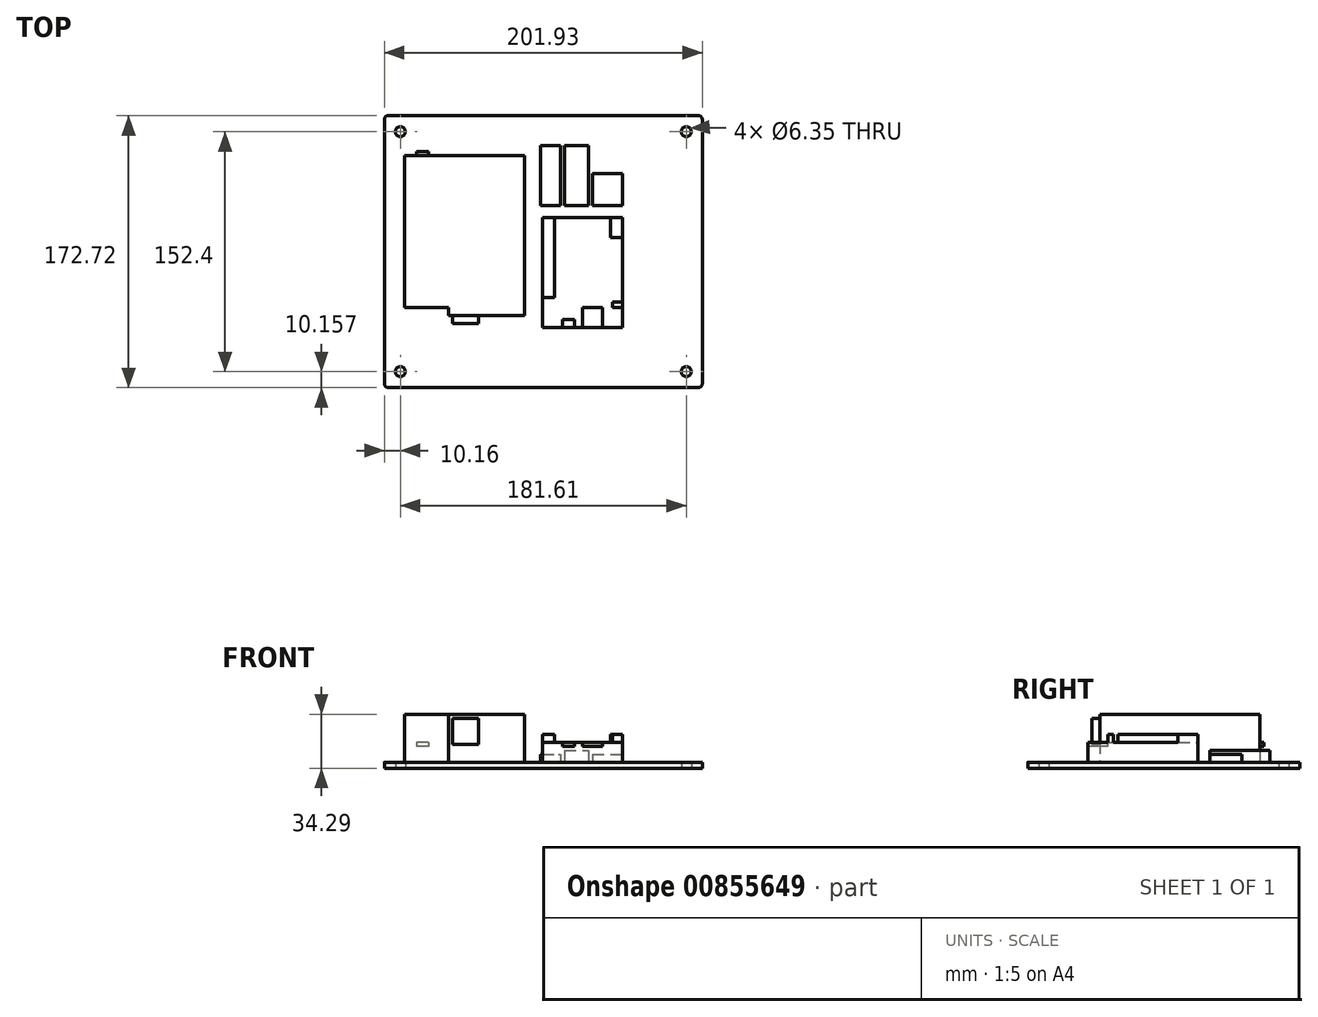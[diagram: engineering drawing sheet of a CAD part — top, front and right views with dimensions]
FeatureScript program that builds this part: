
annotation { "Feature Type Name" : "Feature", "Feature Type Description" : "" }
export const myFeature = defineFeature(function(context is Context, id is Id, definition is map)
    precondition{}
    {
        {
            var Q0;
            Q0=qCreatedBy(makeId("Top.planeOp"),FACE);
            var sketch = newSketch(context, id + "F0", { "sketchPlane" : qUnion([Q0])});
            skLineSegment(sketch, "E0.bottom", {"start": v(-98.77, 92.95) * mm, "end": v(98.08, 92.95) * mm});
            skLineSegment(sketch, "E0.top", {"start": v(-98.77, -79.77) * mm, "end": v(98.08, -79.77) * mm});
            skLineSegment(sketch, "E0.left", {"start": v(-101.3, 90.4) * mm, "end": v(-101.3, -77.23) * mm});
            skLineSegment(sketch, "E0.right", {"start": v(100.62, 90.4) * mm, "end": v(100.62, -77.23) * mm});
            skCircle(sketch, "E1", {"center": v(-91.15, -69.61) * mm, "radius": 3.18 * mm});
            skCircle(sketch, "E2", {"center": v(-91.15, 82.79) * mm, "radius": 3.18 * mm});
            skCircle(sketch, "E3", {"center": v(90.46, 82.79) * mm, "radius": 3.18 * mm});
            skCircle(sketch, "E4", {"center": v(90.46, -69.61) * mm, "radius": 3.18 * mm});
            skPoint(sketch, "E5.visualSharp", {"position": v(-101.3, -79.77) * mm});
            skArc(sketch, "E5.filletArc", {"start": v(-101.3, -77.23) * mm, "mid": v(-100.57, -79.03) * mm, "end": v(-98.77, -79.77) * mm});
            skPoint(sketch, "E6.visualSharp", {"position": v(100.62, -79.77) * mm});
            skArc(sketch, "E6.filletArc", {"start": v(98.08, -79.77) * mm, "mid": v(99.88, -79.03) * mm, "end": v(100.62, -77.23) * mm});
            skPoint(sketch, "E7.visualSharp", {"position": v(100.62, 92.95) * mm});
            skArc(sketch, "E7.filletArc", {"start": v(100.62, 90.4) * mm, "mid": v(99.88, 92.2) * mm, "end": v(98.08, 92.95) * mm});
            skPoint(sketch, "E8.visualSharp", {"position": v(-101.3, 92.95) * mm});
            skArc(sketch, "E8.filletArc", {"start": v(-98.77, 92.95) * mm, "mid": v(-100.57, 92.2) * mm, "end": v(-101.3, 90.4) * mm});
            skSolve(sketch);
        }
        {
            var Q0;
            Q0=makeQuery(id+"F0.imprint","IMPRINT",FACE,{"disambiguationData":[TD([[makeQuery(id+"F0.imprint","IMPRINT",EDGE,{"derivedFrom":sQuery(id+"F0.wireOp",EDGE,"E0.bottom")}),-1.0]])]});
            extrude(context, id + "F1", {"entities" : qUnion([Q0]), "depth" : 3.8 * mm, "offsetDistance" : 25.4 * mm});
        }
        {
            var Q0;
            Q0=makeQuery(id+"F1.opExtrude","CAP_FACE",FACE,{"disambiguationData":[OSD([sQuery(id+"F0.wireOp",EDGE,"E0.bottom"),sQuery(id+"F0.wireOp",EDGE,"E0.top"),sQuery(id+"F0.wireOp",EDGE,"E0.left"),sQuery(id+"F0.wireOp",EDGE,"E0.right")])],"isStart":false});
            var sketch = newSketch(context, id + "F2", { "sketchPlane" : qUnion([Q0])});
            skLineSegment(sketch, "E9.bottom", {"start": v(-88.6, 67.55) * mm, "end": v(-12.4, 67.55) * mm});
            skLineSegment(sketch, "E9.right", {"start": v(-12.4, 67.55) * mm, "end": v(-12.4, -34.05) * mm});
            skLineSegment(sketch, "E10.bottom", {"start": v(-0.98, 28.18) * mm, "end": v(49.82, 28.18) * mm});
            skLineSegment(sketch, "E10.top", {"start": v(-0.98, -41.67) * mm, "end": v(49.82, -41.67) * mm});
            skLineSegment(sketch, "E10.left", {"start": v(-0.98, 28.18) * mm, "end": v(-0.98, -41.67) * mm});
            skLineSegment(sketch, "E10.right", {"start": v(49.82, 28.18) * mm, "end": v(49.82, -41.67) * mm});
            skLineSegment(sketch, "E11.bottom", {"start": v(-2.25, 73.9) * mm, "end": v(10.45, 73.9) * mm});
            skLineSegment(sketch, "E11.top", {"start": v(-2.25, 35.8) * mm, "end": v(10.45, 35.8) * mm});
            skLineSegment(sketch, "E11.left", {"start": v(-2.25, 73.9) * mm, "end": v(-2.25, 35.8) * mm});
            skLineSegment(sketch, "E11.right", {"start": v(10.45, 73.9) * mm, "end": v(10.45, 35.8) * mm});
            skLineSegment(sketch, "E12.bottom", {"start": v(13, 73.9) * mm, "end": v(28.23, 73.9) * mm});
            skLineSegment(sketch, "E12.top", {"start": v(13, 35.8) * mm, "end": v(28.23, 35.8) * mm});
            skLineSegment(sketch, "E12.left", {"start": v(13, 73.9) * mm, "end": v(13, 35.8) * mm});
            skLineSegment(sketch, "E12.right", {"start": v(28.23, 73.9) * mm, "end": v(28.23, 35.8) * mm});
            skLineSegment(sketch, "E13.bottom", {"start": v(30.77, 56.12) * mm, "end": v(49.82, 56.12) * mm});
            skLineSegment(sketch, "E13.top", {"start": v(30.77, 35.8) * mm, "end": v(49.82, 35.8) * mm});
            skLineSegment(sketch, "E13.left", {"start": v(30.77, 56.12) * mm, "end": v(30.77, 35.8) * mm});
            skLineSegment(sketch, "E13.right", {"start": v(49.82, 56.12) * mm, "end": v(49.82, 35.8) * mm});
            skLineSegment(sketch, "E14", {"start": v(-60.67, -34.05) * mm, "end": v(-60.67, -28.97) * mm});
            skLineSegment(sketch, "E15", {"start": v(-60.67, -28.97) * mm, "end": v(-88.6, -28.97) * mm});
            skLineSegment(sketch, "E16", {"start": v(-88.6, 67.55) * mm, "end": v(-88.6, -28.97) * mm});
            skLineSegment(sketch, "E17", {"start": v(-60.67, -34.05) * mm, "end": v(-12.4, -34.05) * mm});
            skSolve(sketch);
        }
        {
            var Q0;
            Q0=makeQuery(id+"F2.imprint","IMPRINT",FACE,{"disambiguationData":[TD([[makeQuery(id+"F2.imprint","IMPRINT",EDGE,{"derivedFrom":sQuery(id+"F2.wireOp",EDGE,"E9.bottom")}),-1.0]])]});
            extrude(context, id + "F3", {"entities" : qUnion([Q0]), "operationType" : NewBodyOperationType.ADD, "depth" : 30.48 * mm, "offsetDistance" : 25.4 * mm});
        }
        {
            var Q0;
            Q0=makeQuery(id+"F2.imprint","IMPRINT",FACE,{"disambiguationData":[TD([[makeQuery(id+"F2.imprint","IMPRINT",EDGE,{"derivedFrom":sQuery(id+"F2.wireOp",EDGE,"E10.bottom")}),-1.0]])]});
            extrude(context, id + "F4", {"entities" : qUnion([Q0]), "operationType" : NewBodyOperationType.ADD, "depth" : 12.7 * mm, "offsetDistance" : 25.4 * mm});
        }
        {
            var Q0;
            Q0=makeQuery(id+"F2.imprint","IMPRINT",FACE,{"disambiguationData":[TD([[makeQuery(id+"F2.imprint","IMPRINT",EDGE,{"derivedFrom":sQuery(id+"F2.wireOp",EDGE,"E13.bottom")}),-1.0]])]});
            extrude(context, id + "F5", {"entities" : qUnion([Q0]), "operationType" : NewBodyOperationType.ADD, "depth" : 5.08 * mm, "offsetDistance" : 25.4 * mm});
        }
        {
            var Q0;
            Q0=makeQuery(id+"F2.imprint","IMPRINT",FACE,{"disambiguationData":[TD([[makeQuery(id+"F2.imprint","IMPRINT",EDGE,{"derivedFrom":sQuery(id+"F2.wireOp",EDGE,"E12.bottom")}),-1.0]])]});
            extrude(context, id + "F6", {"entities" : qUnion([Q0]), "operationType" : NewBodyOperationType.ADD, "depth" : 7.62 * mm, "offsetDistance" : 25.4 * mm});
        }
        {
            var Q0;
            Q0=makeQuery(id+"F2.imprint","IMPRINT",FACE,{"disambiguationData":[TD([[makeQuery(id+"F2.imprint","IMPRINT",EDGE,{"derivedFrom":sQuery(id+"F2.wireOp",EDGE,"E11.bottom")}),-1.0]])]});
            extrude(context, id + "F7", {"entities" : qUnion([Q0]), "operationType" : NewBodyOperationType.ADD, "depth" : 5.08 * mm, "offsetDistance" : 25.4 * mm});
        }
        {
            var Q0;
            Q0=makeQuery(id+"F3.opExtrude","SWEPT_FACE",FACE,{"disambiguationData":[OSD([sQuery(id+"F2.wireOp",EDGE,"E17")])]});
            var sketch = newSketch(context, id + "F8", { "sketchPlane" : qUnion([Q0])});
            skLineSegment(sketch, "E18.bottom", {"start": v(-58.13, 31.75) * mm, "end": v(-41.62, 31.75) * mm});
            skLineSegment(sketch, "E18.top", {"start": v(-58.13, 15.24) * mm, "end": v(-41.62, 15.24) * mm});
            skLineSegment(sketch, "E18.left", {"start": v(-58.13, 31.75) * mm, "end": v(-58.13, 15.24) * mm});
            skLineSegment(sketch, "E18.right", {"start": v(-41.62, 31.75) * mm, "end": v(-41.62, 15.24) * mm});
            skSolve(sketch);
        }
        {
            var Q0;
            Q0=makeQuery(id+"F8.imprint","IMPRINT",FACE,{"disambiguationData":[TD([[makeQuery(id+"F8.imprint","IMPRINT",EDGE,{"derivedFrom":sQuery(id+"F8.wireOp",EDGE,"E18.bottom")}),-1.0]])]});
            extrude(context, id + "F9", {"entities" : qUnion([Q0]), "operationType" : NewBodyOperationType.ADD, "depth" : 5.08 * mm, "offsetDistance" : 25.4 * mm});
        }
        {
            var Q0;
            Q0=makeQuery(id+"F3.opExtrude","SWEPT_FACE",FACE,{"disambiguationData":[OSD([sQuery(id+"F2.wireOp",EDGE,"E9.bottom")])]});
            var sketch = newSketch(context, id + "F10", { "sketchPlane" : qUnion([Q0])});
            skLineSegment(sketch, "E19.bottom", {"start": v(73.37, 16.51) * mm, "end": v(80.99, 16.51) * mm});
            skLineSegment(sketch, "E19.top", {"start": v(73.37, 13.97) * mm, "end": v(80.99, 13.97) * mm});
            skLineSegment(sketch, "E19.left", {"start": v(73.37, 16.51) * mm, "end": v(73.37, 13.97) * mm});
            skLineSegment(sketch, "E19.right", {"start": v(80.99, 16.51) * mm, "end": v(80.99, 13.97) * mm});
            skSolve(sketch);
        }
        {
            var Q0;
            Q0=makeQuery(id+"F10.imprint","IMPRINT",FACE,{"disambiguationData":[TD([[makeQuery(id+"F10.imprint","IMPRINT",EDGE,{"derivedFrom":sQuery(id+"F10.wireOp",EDGE,"E19.bottom")}),-1.0]])]});
            extrude(context, id + "F11", {"entities" : qUnion([Q0]), "operationType" : NewBodyOperationType.ADD, "depth" : 2.54 * mm, "offsetDistance" : 25.4 * mm});
        }
        {
            var Q0;
            Q0=makeQuery(id+"F4.opExtrude","CAP_FACE",FACE,{"disambiguationData":[OSD([sQuery(id+"F2.wireOp",EDGE,"E10.bottom"),sQuery(id+"F2.wireOp",EDGE,"E10.top"),sQuery(id+"F2.wireOp",EDGE,"E10.left"),sQuery(id+"F2.wireOp",EDGE,"E10.right")])],"isStart":false});
            var sketch = newSketch(context, id + "F12", { "sketchPlane" : qUnion([Q0])});
            skLineSegment(sketch, "E20.bottom", {"start": v(6.64, -22.62) * mm, "end": v(-0.98, -22.62) * mm});
            skLineSegment(sketch, "E20.top", {"start": v(6.64, 28.18) * mm, "end": v(-0.98, 28.18) * mm});
            skLineSegment(sketch, "E20.left", {"start": v(6.64, -22.62) * mm, "end": v(6.64, 28.18) * mm});
            skLineSegment(sketch, "E20.right", {"start": v(-0.98, -22.62) * mm, "end": v(-0.98, 28.18) * mm});
            skLineSegment(sketch, "E21.bottom", {"start": v(49.82, 15.48) * mm, "end": v(42.2, 15.48) * mm});
            skLineSegment(sketch, "E21.top", {"start": v(49.82, 28.18) * mm, "end": v(42.2, 28.18) * mm});
            skLineSegment(sketch, "E21.left", {"start": v(49.82, 15.48) * mm, "end": v(49.82, 28.18) * mm});
            skLineSegment(sketch, "E21.right", {"start": v(42.2, 15.48) * mm, "end": v(42.2, 28.18) * mm});
            skSolve(sketch);
        }
        {
            var Q0;
            Q0=makeQuery(id+"F12.imprint","IMPRINT",FACE,{"disambiguationData":[TD([[makeQuery(id+"F12.imprint","IMPRINT",EDGE,{"derivedFrom":sQuery(id+"F12.wireOp",EDGE,"E21.bottom")}),-1.0]])]});
            var Q1;
            Q1=makeQuery(id+"F12.imprint","IMPRINT",FACE,{"disambiguationData":[TD([[makeQuery(id+"F12.imprint","IMPRINT",EDGE,{"derivedFrom":sQuery(id+"F12.wireOp",EDGE,"E20.bottom")}),-1.0]])]});
            extrude(context, id + "F13", {"entities" : qUnion([Q0, Q1]), "operationType" : NewBodyOperationType.ADD, "depth" : 5.08 * mm, "offsetDistance" : 25.4 * mm});
        }
        {
            var Q0;
            Q0=makeQuery(id+"F4.opExtrude","CAP_FACE",FACE,{"disambiguationData":[OSD([sQuery(id+"F2.wireOp",EDGE,"E10.bottom"),sQuery(id+"F2.wireOp",EDGE,"E10.top"),sQuery(id+"F2.wireOp",EDGE,"E10.left"),sQuery(id+"F2.wireOp",EDGE,"E10.right")])],"isStart":false});
            var sketch = newSketch(context, id + "F14", { "sketchPlane" : qUnion([Q0])});
            skLineSegment(sketch, "E22.bottom", {"start": v(49.82, -28.97) * mm, "end": v(43.47, -28.97) * mm});
            skLineSegment(sketch, "E22.top", {"start": v(49.82, -25.3) * mm, "end": v(43.47, -25.3) * mm});
            skLineSegment(sketch, "E22.left", {"start": v(49.82, -28.97) * mm, "end": v(49.82, -25.3) * mm});
            skLineSegment(sketch, "E22.right", {"start": v(43.47, -28.97) * mm, "end": v(43.47, -25.3) * mm});
            skSolve(sketch);
        }
        {
            var Q0;
            Q0=makeQuery(id+"F14.imprint","IMPRINT",FACE,{"disambiguationData":[TD([[makeQuery(id+"F14.imprint","IMPRINT",EDGE,{"derivedFrom":sQuery(id+"F14.wireOp",EDGE,"E22.bottom")}),-1.0]])]});
            extrude(context, id + "F15", {"entities" : qUnion([Q0]), "operationType" : NewBodyOperationType.ADD, "depth" : 5.08 * mm, "offsetDistance" : 25.4 * mm});
        }
        {
            var Q0;
            Q0=makeQuery(id+"F4.opExtrude","CAP_FACE",FACE,{"disambiguationData":[OSD([sQuery(id+"F2.wireOp",EDGE,"E10.bottom"),sQuery(id+"F2.wireOp",EDGE,"E10.top"),sQuery(id+"F2.wireOp",EDGE,"E10.left"),sQuery(id+"F2.wireOp",EDGE,"E10.right")])],"isStart":false});
            var sketch = newSketch(context, id + "F16", { "sketchPlane" : qUnion([Q0])});
            skLineSegment(sketch, "E23.bottom", {"start": v(24.42, -28.97) * mm, "end": v(37.12, -28.97) * mm});
            skLineSegment(sketch, "E23.top", {"start": v(24.42, -41.67) * mm, "end": v(37.12, -41.67) * mm});
            skLineSegment(sketch, "E23.left", {"start": v(24.42, -28.97) * mm, "end": v(24.42, -41.67) * mm});
            skLineSegment(sketch, "E23.right", {"start": v(37.12, -28.97) * mm, "end": v(37.12, -41.67) * mm});
            skSolve(sketch);
        }
        {
            var Q0;
            Q0=makeQuery(id+"F16.imprint","IMPRINT",FACE,{"disambiguationData":[TD([[makeQuery(id+"F16.imprint","IMPRINT",EDGE,{"derivedFrom":sQuery(id+"F16.wireOp",EDGE,"E23.bottom")}),-1.0]])]});
            extrude(context, id + "F17", {"entities" : qUnion([Q0]), "operationType" : NewBodyOperationType.REMOVE, "oppositeDirection" : true, "depth" : 2.54 * mm, "offsetDistance" : 25.4 * mm});
        }
        {
            var Q0;
            Q0=makeQuery(id+"F4.opExtrude","CAP_FACE",FACE,{"disambiguationData":[OSD([sQuery(id+"F2.wireOp",EDGE,"E10.bottom"),sQuery(id+"F2.wireOp",EDGE,"E10.top"),sQuery(id+"F2.wireOp",EDGE,"E10.left"),sQuery(id+"F2.wireOp",EDGE,"E10.right")])],"isStart":false});
            var sketch = newSketch(context, id + "F18", { "sketchPlane" : qUnion([Q0])});
            skLineSegment(sketch, "E24.bottom", {"start": v(11.72, -36.6) * mm, "end": v(19.34, -36.6) * mm});
            skLineSegment(sketch, "E24.top", {"start": v(11.72, -41.67) * mm, "end": v(19.34, -41.67) * mm});
            skLineSegment(sketch, "E24.left", {"start": v(11.72, -36.6) * mm, "end": v(11.72, -41.67) * mm});
            skLineSegment(sketch, "E24.right", {"start": v(19.34, -36.6) * mm, "end": v(19.34, -41.67) * mm});
            skSolve(sketch);
        }
        {
            var Q0;
            Q0 = qSketchRegion(id + "F18", true);
            extrude(context, id + "F19", {"entities" : qUnion([Q0]), "operationType" : NewBodyOperationType.REMOVE, "oppositeDirection" : true, "depth" : 2.54 * mm, "offsetDistance" : 25.4 * mm});
        }
    });
